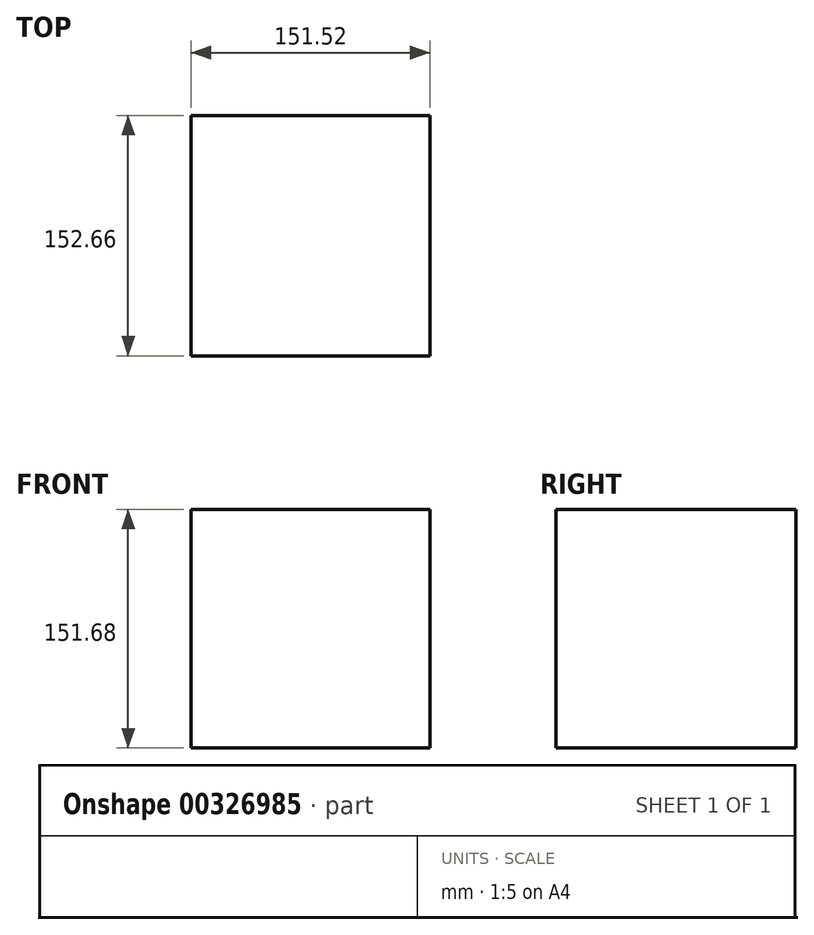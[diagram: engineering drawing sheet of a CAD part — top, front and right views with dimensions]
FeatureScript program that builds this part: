
annotation { "Feature Type Name" : "Feature", "Feature Type Description" : "" }
export const myFeature = defineFeature(function(context is Context, id is Id, definition is map)
    precondition{}
    {
        {
            var Q0;
            Q0=qCreatedBy(makeId("Top.planeOp"),FACE);
            var sketch = newSketch(context, id + "F0", { "sketchPlane" : qUnion([Q0])});
            skLineSegment(sketch, "E0.bottom", {"start": v(-75.76, 76.33) * mm, "end": v(75.76, 76.33) * mm});
            skLineSegment(sketch, "E0.top", {"start": v(-75.76, -76.33) * mm, "end": v(75.76, -76.33) * mm});
            skLineSegment(sketch, "E0.left", {"start": v(-75.76, 76.33) * mm, "end": v(-75.76, -76.33) * mm});
            skLineSegment(sketch, "E0.right", {"start": v(75.76, 76.33) * mm, "end": v(75.76, -76.33) * mm});
            skSolve(sketch);
        }
        {
            var Q0;
            Q0=makeQuery(id+"F0.imprint","IMPRINT",FACE,{"disambiguationData":[TD([[makeQuery(id+"F0.imprint","IMPRINT",EDGE,{"derivedFrom":sQuery(id+"F0.wireOp",EDGE,"E0.bottom")}),-1.0]])]});
            var sketch = newSketch(context, id + "F1", { "sketchPlane" : qUnion([Q0])});
            skSolve(sketch);
        }
        {
            var Q0;
            Q0=makeQuery(id+"F1.imprint","IMPRINT",FACE,{"disambiguationData":[TD([[makeQuery(id+"F1.imprint","IMPRINT",EDGE,{"derivedFrom":makeQuery(id+"F0.imprint","IMPRINT",EDGE,{"derivedFrom":sQuery(id+"F0.wireOp",EDGE,"E0.bottom")})}),-1.0]])]});
            extrude(context, id + "F2", {"entities" : qUnion([Q0]), "depth" : 76.2 * mm});
        }
        {
            var Q0;
            Q0=makeQuery(id+"F0.imprint","IMPRINT",FACE,{"disambiguationData":[TD([[makeQuery(id+"F0.imprint","IMPRINT",EDGE,{"derivedFrom":sQuery(id+"F0.wireOp",EDGE,"E0.bottom")}),-1.0]])]});
            extrude(context, id + "F3", {"entities" : qUnion([Q0]), "operationType" : NewBodyOperationType.ADD, "oppositeDirection" : true, "depth" : 75.5 * mm});
        }
    });
